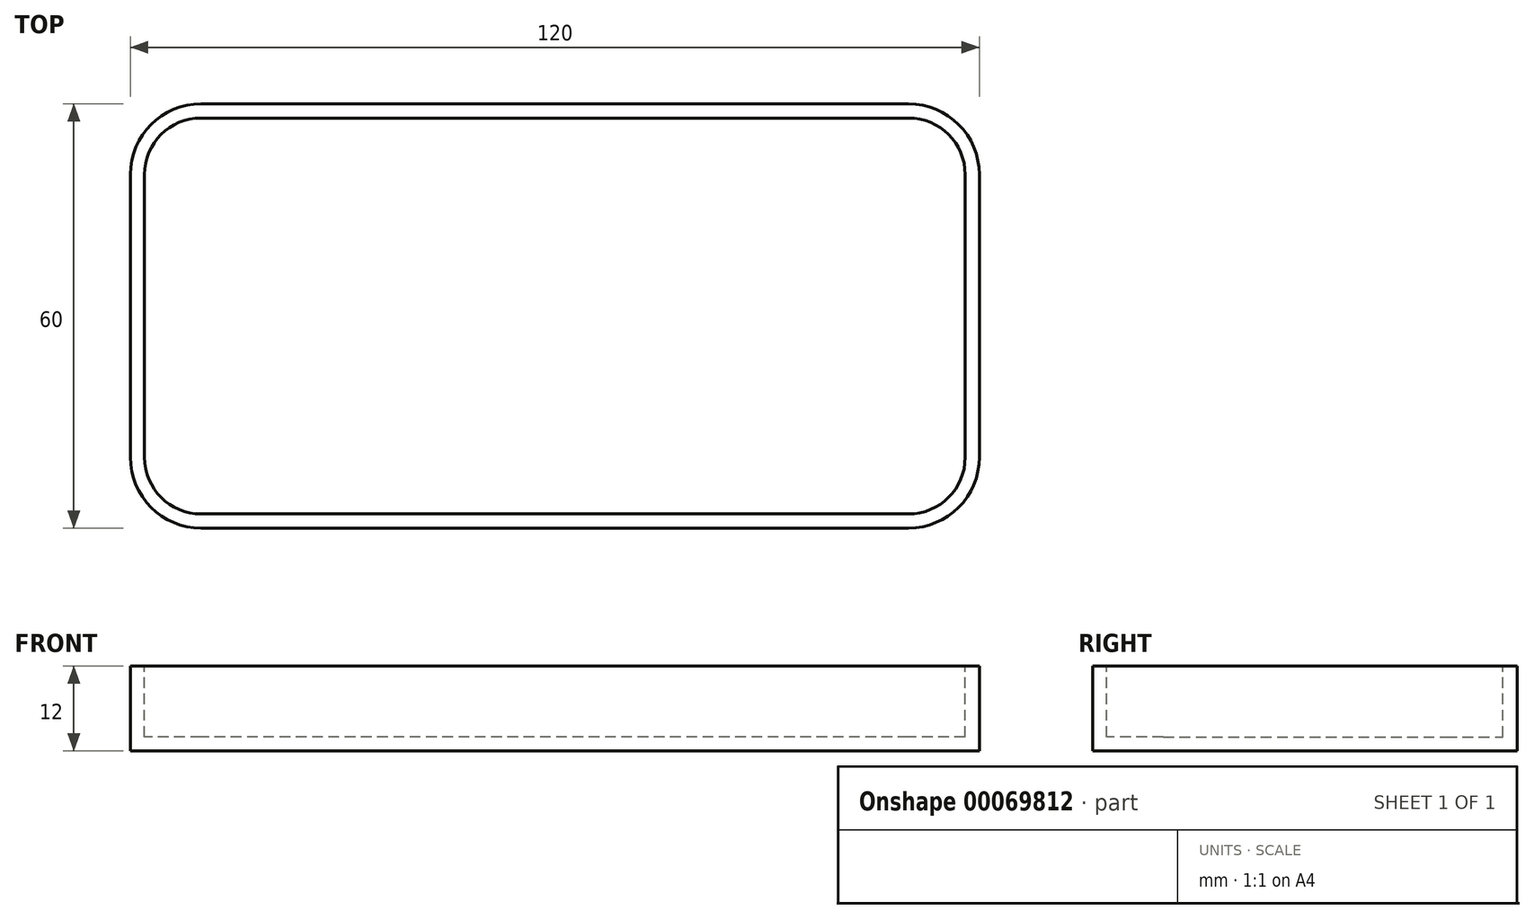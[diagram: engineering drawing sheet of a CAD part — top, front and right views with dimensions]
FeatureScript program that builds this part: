
annotation { "Feature Type Name" : "Feature", "Feature Type Description" : "" }
export const myFeature = defineFeature(function(context is Context, id is Id, definition is map)
    precondition{}
    {
        {
            var Q0;
            Q0=qCreatedBy(makeId("Top.planeOp"),FACE);
            var sketch = newSketch(context, id + "F0", { "sketchPlane" : qUnion([Q0])});
            skLineSegment(sketch, "E0.bottom", {"start": v(-52.24, 23.6) * mm, "end": v(67.76, 23.6) * mm});
            skLineSegment(sketch, "E0.top", {"start": v(-52.24, -36.4) * mm, "end": v(67.76, -36.4) * mm});
            skLineSegment(sketch, "E0.left", {"start": v(-52.24, 23.6) * mm, "end": v(-52.24, -36.4) * mm});
            skLineSegment(sketch, "E0.right", {"start": v(67.76, 23.6) * mm, "end": v(67.76, -36.4) * mm});
            skSolve(sketch);
        }
        {
            var Q0;
            Q0=makeQuery(id+"F0.imprint","IMPRINT",FACE,{"disambiguationData":[TD([[makeQuery(id+"F0.imprint","IMPRINT",EDGE,{"derivedFrom":sQuery(id+"F0.wireOp",EDGE,"E0.bottom")}),-1.0]])]});
            extrude(context, id + "F1", {"entities" : qUnion([Q0]), "depth" : 12 * mm});
        }
        {
            var Q0;
            Q0=makeQuery(id+"F1.opExtrude","SWEPT_EDGE",EDGE,{"disambiguationData":[OSD([sQuery(id+"F0.wireOp",EDGE,"E0.top"),sQuery(id+"F0.wireOp",EDGE,"E0.left")])]});
            var Q1;
            Q1=makeQuery(id+"F1.opExtrude","SWEPT_EDGE",EDGE,{"disambiguationData":[OSD([sQuery(id+"F0.wireOp",EDGE,"E0.top"),sQuery(id+"F0.wireOp",EDGE,"E0.right")])]});
            var Q2;
            Q2=makeQuery(id+"F1.opExtrude","SWEPT_EDGE",EDGE,{"disambiguationData":[OSD([sQuery(id+"F0.wireOp",EDGE,"E0.bottom"),sQuery(id+"F0.wireOp",EDGE,"E0.right")])]});
            var Q3;
            Q3=makeQuery(id+"F1.opExtrude","SWEPT_EDGE",EDGE,{"disambiguationData":[OSD([sQuery(id+"F0.wireOp",EDGE,"E0.bottom"),sQuery(id+"F0.wireOp",EDGE,"E0.left")])]});
            fillet(context, id + "F2", {"entities" : qUnion([Q0, Q1, Q2, Q3]), "radius" : 10 * mm, "tangentPropagation" : true, "allowEdgeOverflow" : false});
        }
        {
            var Q0;
            Q0=makeQuery(id+"F1.opExtrude","CAP_FACE",FACE,{"disambiguationData":[OSD([sQuery(id+"F0.wireOp",EDGE,"E0.bottom"),sQuery(id+"F0.wireOp",EDGE,"E0.top"),sQuery(id+"F0.wireOp",EDGE,"E0.left"),sQuery(id+"F0.wireOp",EDGE,"E0.right")])],"isStart":false});
            var sketch = newSketch(context, id + "F3", { "sketchPlane" : qUnion([Q0])});
            skArc(sketch, "E1.0", {"start": v(65.76, 13.6) * mm, "mid": v(63.42, 19.25) * mm, "end": v(57.76, 21.6) * mm});
            skLineSegment(sketch, "E1.1", {"start": v(65.76, -26.4) * mm, "end": v(65.76, 13.6) * mm});
            skLineSegment(sketch, "E1.2", {"start": v(57.76, 21.6) * mm, "end": v(-42.24, 21.6) * mm});
            skArc(sketch, "E1.3", {"start": v(57.76, -34.4) * mm, "mid": v(63.42, -32.06) * mm, "end": v(65.76, -26.4) * mm});
            skArc(sketch, "E1.4", {"start": v(-42.24, 21.6) * mm, "mid": v(-47.9, 19.25) * mm, "end": v(-50.24, 13.6) * mm});
            skLineSegment(sketch, "E1.5", {"start": v(-50.24, 13.6) * mm, "end": v(-50.24, -26.4) * mm});
            skArc(sketch, "E1.6", {"start": v(-50.24, -26.4) * mm, "mid": v(-47.9, -32.06) * mm, "end": v(-42.24, -34.4) * mm});
            skLineSegment(sketch, "E1.7", {"start": v(-42.24, -34.4) * mm, "end": v(57.76, -34.4) * mm});
            skSolve(sketch);
        }
        {
            var Q0;
            Q0=makeQuery(id+"F3.imprint","IMPRINT",FACE,{"disambiguationData":[TD([[makeQuery(id+"F3.imprint","IMPRINT",EDGE,{"derivedFrom":sQuery(id+"F3.wireOp",EDGE,"E1.0")}),1.0]])]});
            extrude(context, id + "F4", {"entities" : qUnion([Q0]), "operationType" : NewBodyOperationType.REMOVE, "oppositeDirection" : true, "depth" : 10 * mm});
        }
    });
